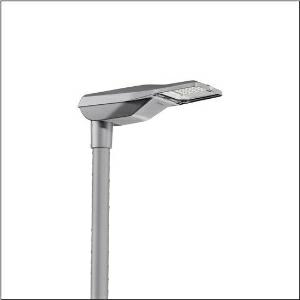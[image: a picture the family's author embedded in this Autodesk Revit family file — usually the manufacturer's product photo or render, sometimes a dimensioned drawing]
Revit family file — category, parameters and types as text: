
# Revit family: streetlight_sl_21_iq_micro___st0_8a_5xe1c61d08cb_7ac8
name_source: partatom
category: Lighting Fixtures
units: mm (PartAtom-declared; Revit-internal decimal feet)

## family parameters
Cut with Voids When Loaded = No
Host = Face
Light Source = No
Part Type = Normal
Room Calculation Point = No
Round Connector Dimension = Use Diameter
Shared = No

## types (1)
- --- (1 x LED, 2570 lm, 19.4 W, 2700K)
    Apparent Load = 19 VA
    CIE Flux Codes = 38 75 97 100 100
    Color Rendering = 70
    Color Temperature = 2700K
    Default Elevation = 1800 mm
    Description = Streetlight SL 21 iQ micro, mast luminaire, primary light control with lens, of PMMA, primary optical cover: cover, of toughened safety glass, transparent, light distribution: ST0.8a, light emission: direct distribution, primary light characteristic: asymmetric, installation type: post-top, side-entry, LED, High Power LED, rated luminous flux: 2.570lm, luminous efficacy: 133lm/W, light colour: 727, colour temperature: 2700K, control gear: iQ-Comfort, control: Auto-Match, Temp-Guard, Lumen-Switch, Night-Set, Smart-Wire, Light-Fading, Desk-Remote (wireless, voltage-free reading and setting of iQ features in the workshop via application-optimized NFC function/RFID function), optimised constant luminous flux control (CLO 2.0), pre-setting: linear dimming characteristic, mains connection: 220..240V, AC, 50/60Hz, start of lifetime: 19W, end of service life: 20W, reduction: 10W, luminaire housing, of diecast aluminium, powder-coated, SITECO metallic grey (DB 702S), corrosivity category C5 high according to DIN EN ISO 12944, please order mast flange separately, inclination adjustable: 0°, 5°, 10°, 15°, sealing non-destructively replaceable, multi-level sealing system, length: 528mm, width: 235mm, height: 110mm, mast flange for spigot size: 42mm (side-entry): 5XC10008XM4, 60/48mm (side-entry/post-top): 5XC10108XM2, 76/60mm (side-entry/post-top): 5XC10108XM1, protection rating (complete): IP66, insulation class (complete): insulation class II (safety insulation), certification: CE, ENEC, ENEC+, VDE, impact resistance: IK10, permissible operating ambient temperature for outdoor applications: -40..+50°C, standard-compliant lighting for roads and squares, packaging unit: 1 piece

Light Distribution: ST0.8a
    Height = 110 mm
    Lamp = 1 x LED
    Lamp Light Flux = 2570 lm
    Lamp Power = 19.4 W
    Lamp count = 1
    Length = 528 mm
    Luminous efficacy = 132 lm/W
    Manufacturer = Siteco
    ModVariant = No
    Model = 5XE1C61D08CB
    Number of Poles = 1
    OnlyDefault = Yes
    Power Factor = 1
    Product Name = Streetlight SL 21 iQ micro | ST0.8a
    Product group = mast luminaire | pylon top
    ProductGroupID = 6100
    Protection Class = Protection class II
    Protection Degree = IP 66
    RLX_Detail_Level = 1
    RLX_Emergency_Light_Flux = 0 lm
    RLX_Emergency_Type = 0
    RLX_Emergency_Type_DB = No
    RlxData = <blob elided: 98965 chars, md5=56f8db7e>
    Socket = socket
    Standby Power = 0 W
    System Light Flux = 2570 lm
    System Power = 19 W
    Type Comments = factory setting: luminous flux: 100 % | dim-lin: 254 | 387 mA
    Type Image = l_1006881.jpg
    URL = http://relux.com
    VarID = @adj_137815
    Voltage = 0 V
    Weight = 0.00 kg
    Width = 235 mm

## geometry (parser evidence)
native form markers: Blend x4, Sweep x10
no freeform markers — native parametric forms only
